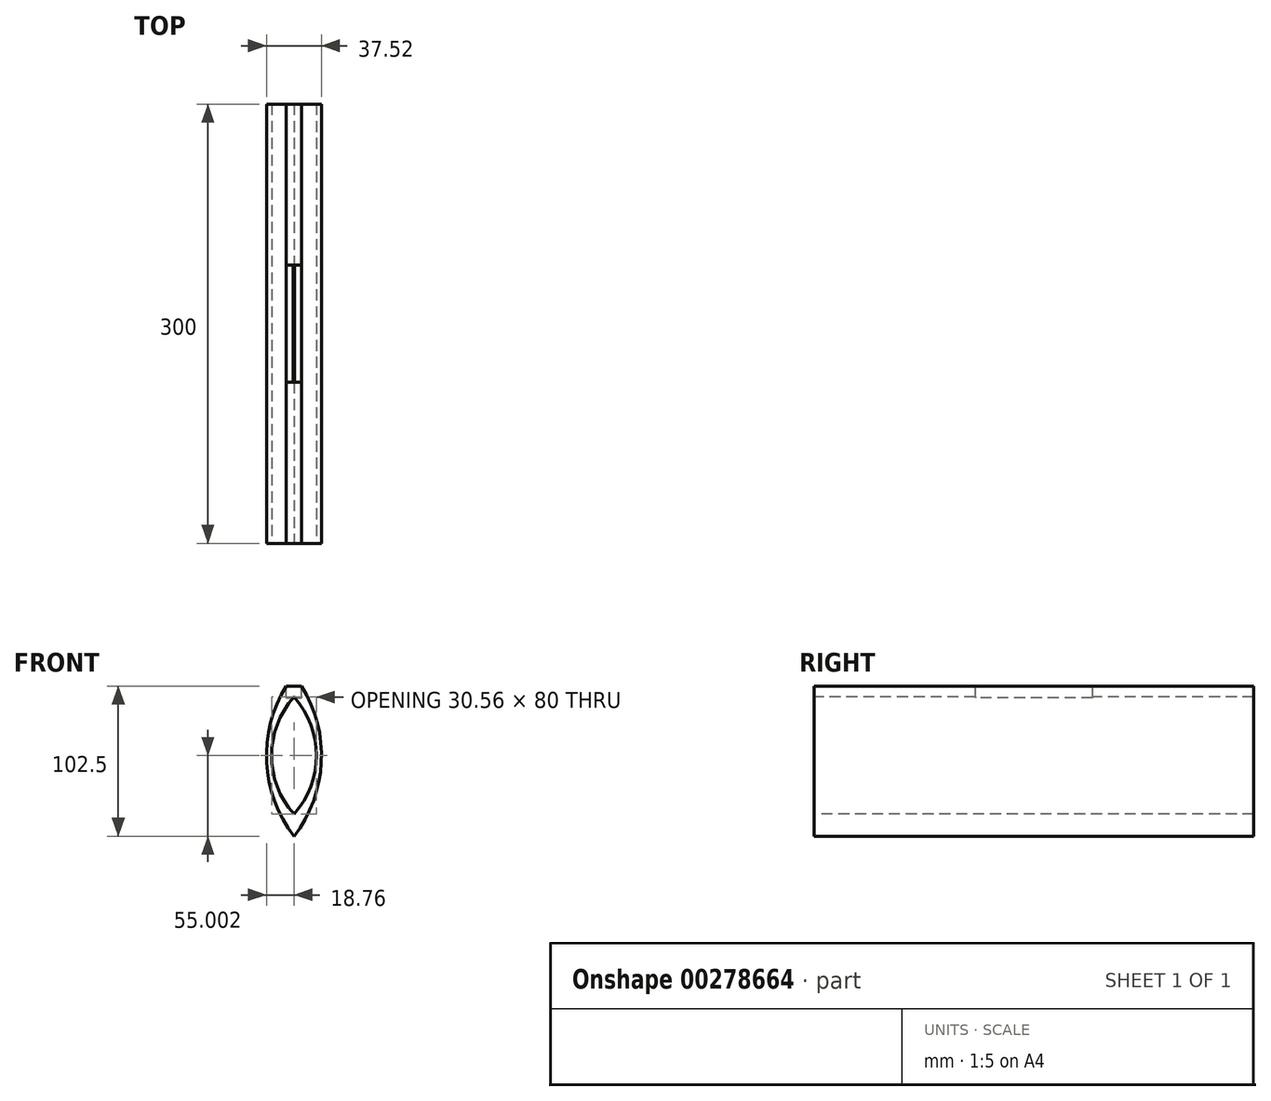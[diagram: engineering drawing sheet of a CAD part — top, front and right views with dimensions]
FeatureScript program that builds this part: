
annotation { "Feature Type Name" : "Feature", "Feature Type Description" : "" }
export const myFeature = defineFeature(function(context is Context, id is Id, definition is map)
    precondition{}
    {
        {
            var Q0;
            Q0=qCreatedBy(makeId("Front.planeOp"),FACE);
            var sketch = newSketch(context, id + "F0", { "sketchPlane" : qUnion([Q0])});
            skArc(sketch, "E0", {"start": v(0, -60.36) * mm, "mid": v(18.76, -5.36) * mm, "end": v(0, 49.64) * mm});
            skArc(sketch, "E1", {"start": v(0, 49.64) * mm, "mid": v(-18.76, -5.36) * mm, "end": v(0, -60.36) * mm});
            skPoint(sketch, "E2.start.orphan", {"position": v(18.6, 0) * mm});
            skSolve(sketch);
        }
        {
            var Q0;
            Q0 = qSketchRegion(id + "F0", true);
            extrude(context, id + "F1", {"entities" : qUnion([Q0]), "depth" : 300 * mm});
        }
        {
            var Q0;
            Q0=makeQuery(id+"F1.opExtrude","CAP_FACE",FACE,{"disambiguationData":[OSD([sQuery(id+"F0.wireOp",EDGE,"E0"),sQuery(id+"F0.wireOp",EDGE,"E1")])],"isStart":false});
            var sketch = newSketch(context, id + "F2", { "sketchPlane" : qUnion([Q0])});
            skArc(sketch, "E3", {"start": v(0, -45.36) * mm, "mid": v(15.28, -5.36) * mm, "end": v(0, 34.64) * mm});
            skArc(sketch, "E4", {"start": v(0, 34.64) * mm, "mid": v(-15.28, -5.36) * mm, "end": v(0, -45.36) * mm});
            skSolve(sketch);
        }
        {
            var Q0;
            Q0 = qSketchRegion(id + "F2", true);
            extrude(context, id + "F3", {"entities" : qUnion([Q0]), "operationType" : NewBodyOperationType.REMOVE, "oppositeDirection" : true, "depth" : 300 * mm});
        }
        {
            var Q0;
            Q0=makeQuery(id+"F1.opExtrude","CAP_FACE",FACE,{"disambiguationData":[OSD([sQuery(id+"F0.wireOp",EDGE,"E0"),sQuery(id+"F0.wireOp",EDGE,"E1")])],"isStart":false});
            var sketch = newSketch(context, id + "F4", { "sketchPlane" : qUnion([Q0])});
            skLineSegment(sketch, "E5.bottom", {"start": v(-38.07, 42.14) * mm, "end": v(35.46, 42.14) * mm});
            skLineSegment(sketch, "E5.top", {"start": v(-38.07, 87.3) * mm, "end": v(35.46, 87.3) * mm});
            skLineSegment(sketch, "E5.left", {"start": v(-38.07, 42.14) * mm, "end": v(-38.07, 87.3) * mm});
            skLineSegment(sketch, "E5.right", {"start": v(35.46, 42.14) * mm, "end": v(35.46, 87.3) * mm});
            skSolve(sketch);
        }
        {
            var Q0;
            Q0 = qSketchRegion(id + "F4", true);
            extrude(context, id + "F5", {"entities" : qUnion([Q0]), "operationType" : NewBodyOperationType.REMOVE, "oppositeDirection" : true, "depth" : 300 * mm});
        }
        {
            var Q0;
            Q0=makeQuery(id+"F5.boolean.opBoolean","COPY",FACE,{"derivedFrom":makeQuery(id+"F5.opExtrude","SWEPT_FACE",FACE,{"disambiguationData":[OSD([sQuery(id+"F4.wireOp",EDGE,"E5.bottom")])]})});
            var sketch = newSketch(context, id + "F6", { "sketchPlane" : qUnion([Q0])});
            skLineSegment(sketch, "E6.bottom", {"start": v(-5.2, -110) * mm, "end": v(5.2, -110) * mm});
            skLineSegment(sketch, "E6.top", {"start": v(-5.2, -190) * mm, "end": v(5.2, -190) * mm});
            skLineSegment(sketch, "E6.left", {"start": v(-5.2, -110) * mm, "end": v(-5.2, -190) * mm});
            skLineSegment(sketch, "E6.right", {"start": v(5.2, -110) * mm, "end": v(5.2, -190) * mm});
            skSolve(sketch);
        }
        {
            var Q0;
            Q0 = qSketchRegion(id + "F6", true);
            extrude(context, id + "F7", {"entities" : qUnion([Q0]), "operationType" : NewBodyOperationType.REMOVE, "oppositeDirection" : true, "depth" : 8 * mm});
        }
    });
